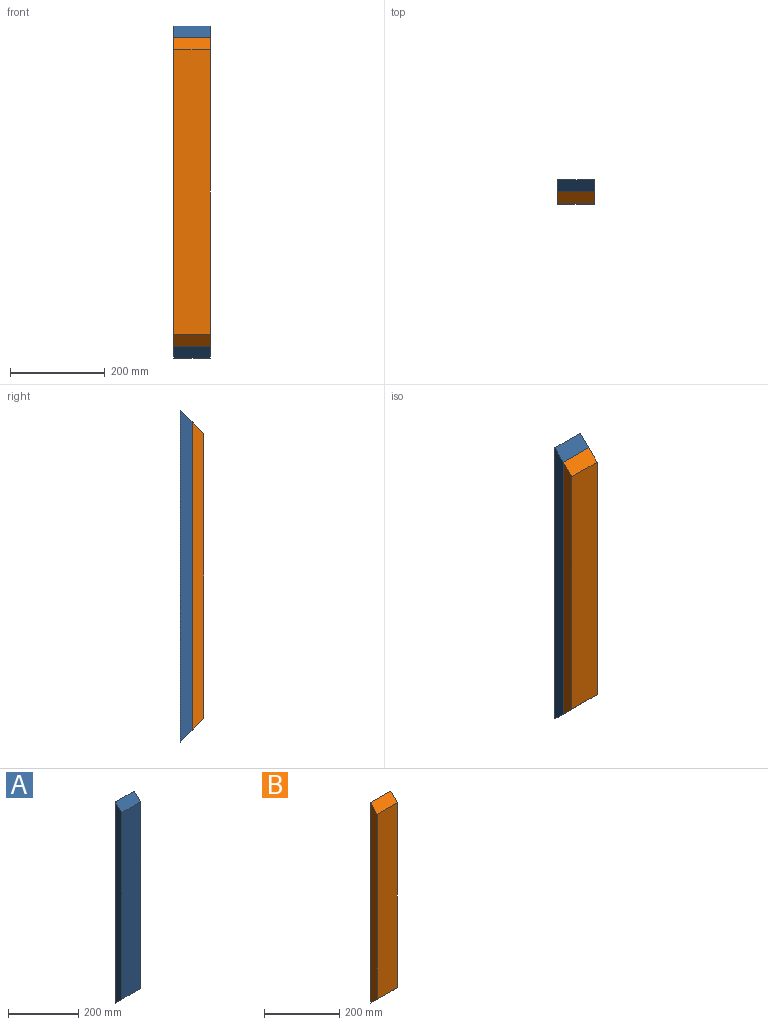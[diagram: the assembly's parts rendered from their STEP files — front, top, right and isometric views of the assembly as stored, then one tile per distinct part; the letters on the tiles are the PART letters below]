
ASSEMBLY  parts=2 mates=1
PART A: 6 faces, bbox 76x25x700 mm
  f0: plane 700x25mm, normal (1,0,0), area 16875mm2, adj f1,f3,f4,f5
  f1: plane 650x76mm, normal (0,-1,0), area 49400mm2, adj f0,f2,f4,f5
  f2: plane 700x25mm, normal (-1,0,0), area 16875mm2, adj f1,f3,f4,f5
  f3: plane 700x76mm, normal (0,1,0), area 53200mm2, adj f0,f2,f4,f5
  f4: plane 76x25mm, normal (0,-0.71,-0.71), area 2687mm2, adj f0,f1,f2,f3
  f5: plane 76x25mm, normal (0,-0.71,0.71), area 2687mm2, adj f0,f1,f2,f3
PART B: 6 faces, bbox 76x25x650 mm
  f0: plane 650x25mm, normal (1,0,0), area 15625mm2, adj f1,f3,f4,f5
  f1: plane 600x76mm, normal (0,-1,0), area 45600mm2, adj f0,f2,f4,f5
  f2: plane 650x25mm, normal (-1,0,0), area 15625mm2, adj f1,f3,f4,f5
  f3: plane 650x76mm, normal (0,1,0), area 49400mm2, adj f0,f2,f4,f5
  f4: plane 76x25mm, normal (0,-0.71,-0.71), area 2687mm2, adj f0,f1,f2,f3
  f5: plane 76x25mm, normal (0,-0.71,0.71), area 2687mm2, adj f0,f1,f2,f3
PLACE A t=(-174.69,-113.74,-121.7)mm
PLACE B t=(-327.74,-138.74,-121.7)mm
MATE fastened B.f3 <-> A.f1  axis (0,1,0) through (-113.93,-138.74,-509.75)mm
